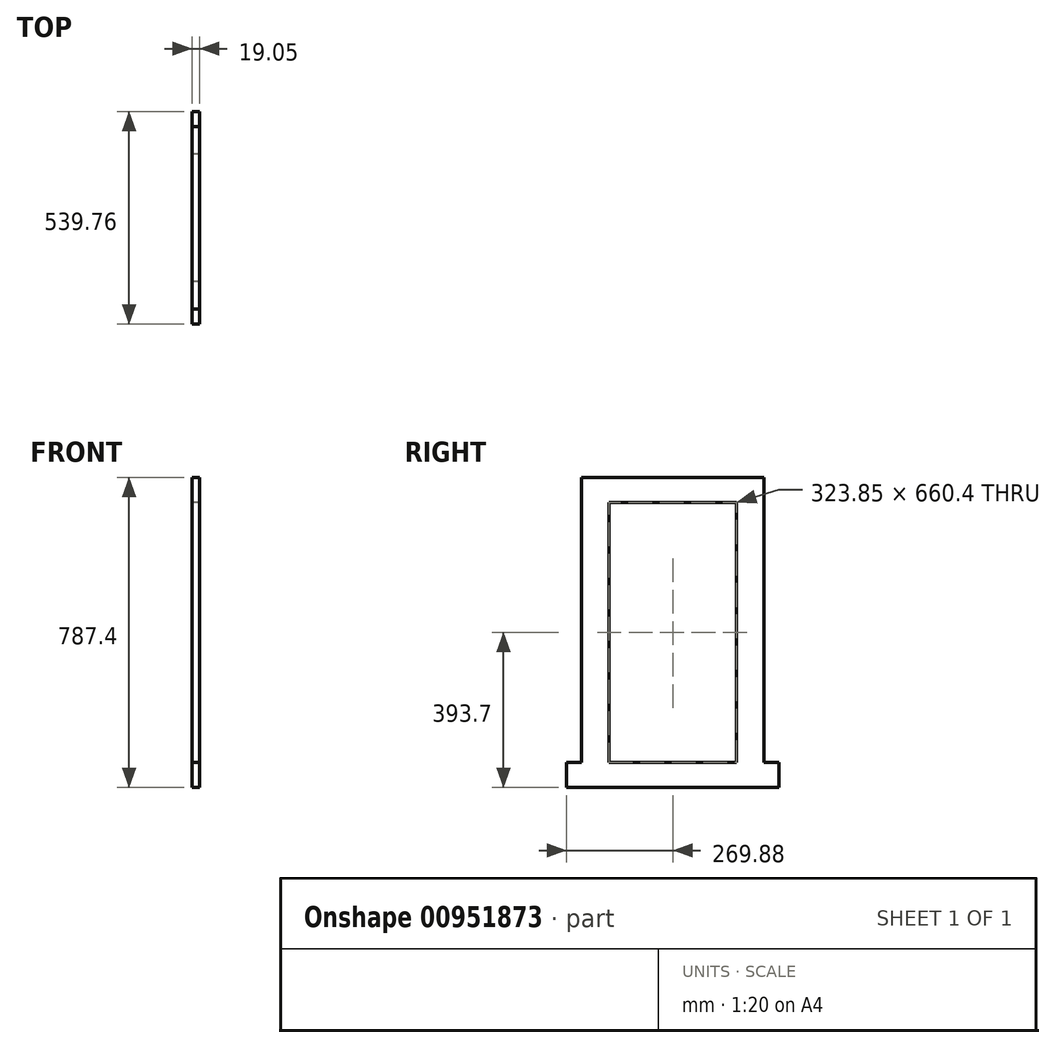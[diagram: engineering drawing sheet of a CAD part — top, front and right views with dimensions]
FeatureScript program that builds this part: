
annotation { "Feature Type Name" : "Feature", "Feature Type Description" : "" }
export const myFeature = defineFeature(function(context is Context, id is Id, definition is map)
    precondition{}
    {
        {
            var Q0;
            Q0=qCreatedBy(makeId("Right.planeOp"),FACE);
            var sketch = newSketch(context, id + "F0", { "sketchPlane" : qUnion([Q0])});
            skLineSegment(sketch, "E0.bottom", {"start": v(269.88, 0) * mm, "end": v(-269.88, 0) * mm});
            skLineSegment(sketch, "E0.top", {"start": v(269.88, 63.5) * mm, "end": v(-269.88, 63.5) * mm});
            skLineSegment(sketch, "E0.left", {"start": v(269.88, 0) * mm, "end": v(269.88, 63.5) * mm});
            skLineSegment(sketch, "E0.right", {"start": v(-269.88, 0) * mm, "end": v(-269.88, 63.5) * mm});
            skSolve(sketch);
        }
        {
            var Q0;
            Q0=qCreatedBy(makeId("Right.planeOp"),FACE);
            var sketch = newSketch(context, id + "F1", { "sketchPlane" : qUnion([Q0])});
            skLineSegment(sketch, "E1.bottom", {"start": v(231.77, 723.9) * mm, "end": v(161.92, 723.9) * mm});
            skLineSegment(sketch, "E1.top", {"start": v(231.78, 63.5) * mm, "end": v(161.92, 63.5) * mm});
            skLineSegment(sketch, "E1.left", {"start": v(231.77, 723.9) * mm, "end": v(231.78, 63.5) * mm});
            skLineSegment(sketch, "E1.right", {"start": v(161.92, 723.9) * mm, "end": v(161.92, 63.5) * mm});
            skSolve(sketch);
        }
        {
            var Q0;
            Q0=qCreatedBy(makeId("Right.planeOp"),FACE);
            var sketch = newSketch(context, id + "F2", { "sketchPlane" : qUnion([Q0])});
            skLineSegment(sketch, "E2.bottom", {"start": v(-161.93, 723.9) * mm, "end": v(-231.78, 723.9) * mm});
            skLineSegment(sketch, "E2.top", {"start": v(-161.93, 63.5) * mm, "end": v(-231.78, 63.5) * mm});
            skLineSegment(sketch, "E2.left", {"start": v(-161.93, 723.9) * mm, "end": v(-161.93, 63.5) * mm});
            skLineSegment(sketch, "E2.right", {"start": v(-231.78, 723.9) * mm, "end": v(-231.78, 63.5) * mm});
            skSolve(sketch);
        }
        {
            var Q0;
            Q0=qCreatedBy(makeId("Right.planeOp"),FACE);
            var sketch = newSketch(context, id + "F3", { "sketchPlane" : qUnion([Q0])});
            skLineSegment(sketch, "E3.bottom", {"start": v(269.88, 0) * mm, "end": v(-269.88, 0) * mm});
            skLineSegment(sketch, "E3.top", {"start": v(269.88, 63.5) * mm, "end": v(-269.88, 63.5) * mm});
            skLineSegment(sketch, "E3.left", {"start": v(269.88, 0) * mm, "end": v(269.88, 63.5) * mm});
            skLineSegment(sketch, "E3.right", {"start": v(-269.88, 0) * mm, "end": v(-269.88, 63.5) * mm});
            skLineSegment(sketch, "E4.bottom", {"start": v(231.77, 723.9) * mm, "end": v(161.92, 723.9) * mm});
            skLineSegment(sketch, "E4.top", {"start": v(231.78, 63.5) * mm, "end": v(161.92, 63.5) * mm});
            skLineSegment(sketch, "E4.left", {"start": v(231.77, 723.9) * mm, "end": v(231.78, 63.5) * mm});
            skLineSegment(sketch, "E4.right", {"start": v(161.92, 723.9) * mm, "end": v(161.92, 63.5) * mm});
            skLineSegment(sketch, "E5.bottom", {"start": v(-161.93, 723.9) * mm, "end": v(-231.78, 723.9) * mm});
            skLineSegment(sketch, "E5.top", {"start": v(-161.93, 63.5) * mm, "end": v(-231.78, 63.5) * mm});
            skLineSegment(sketch, "E5.left", {"start": v(-161.93, 723.9) * mm, "end": v(-161.93, 63.5) * mm});
            skLineSegment(sketch, "E5.right", {"start": v(-231.78, 723.9) * mm, "end": v(-231.78, 63.5) * mm});
            skLineSegment(sketch, "E6.bottom", {"start": v(231.77, 787.4) * mm, "end": v(-231.78, 787.4) * mm});
            skLineSegment(sketch, "E6.top", {"start": v(231.77, 723.9) * mm, "end": v(-231.78, 723.9) * mm});
            skLineSegment(sketch, "E6.left", {"start": v(231.77, 787.4) * mm, "end": v(231.77, 723.9) * mm});
            skLineSegment(sketch, "E6.right", {"start": v(-231.78, 787.4) * mm, "end": v(-231.78, 723.9) * mm});
            skSolve(sketch);
        }
        {
            var Q0;
            Q0=makeQuery(id+"F3.imprint","IMPRINT",FACE,{"disambiguationData":[TD([[makeQuery(id+"F3.imprint","IMPRINT",EDGE,{"derivedFrom":sQuery(id+"F3.wireOp",EDGE,"E4.bottom")}),1.0]])]});
            var Q1;
            Q1=makeQuery(id+"F3.imprint","IMPRINT",FACE,{"disambiguationData":[TD([[makeQuery(id+"F3.imprint","IMPRINT",EDGE,{"derivedFrom":sQuery(id+"F3.wireOp",EDGE,"E5.bottom")}),1.0]])]});
            var Q2;
            Q2=makeQuery(id+"F3.imprint","IMPRINT",FACE,{"disambiguationData":[TD([[makeQuery(id+"F3.imprint","IMPRINT",EDGE,{"derivedFrom":sQuery(id+"F3.wireOp",EDGE,"E4.bottom")}),-1.0]])]});
            var Q3;
            Q3=makeQuery(id+"F3.imprint","IMPRINT",FACE,{"disambiguationData":[TD([[makeQuery(id+"F3.imprint","IMPRINT",EDGE,{"derivedFrom":sQuery(id+"F3.wireOp",EDGE,"E3.bottom")}),-1.0]])]});
            extrude(context, id + "F4", {"entities" : qUnion([Q0, Q1, Q2, Q3]), "depth" : 19.05 * mm, "offsetDistance" : 25.4 * mm});
        }
    });
